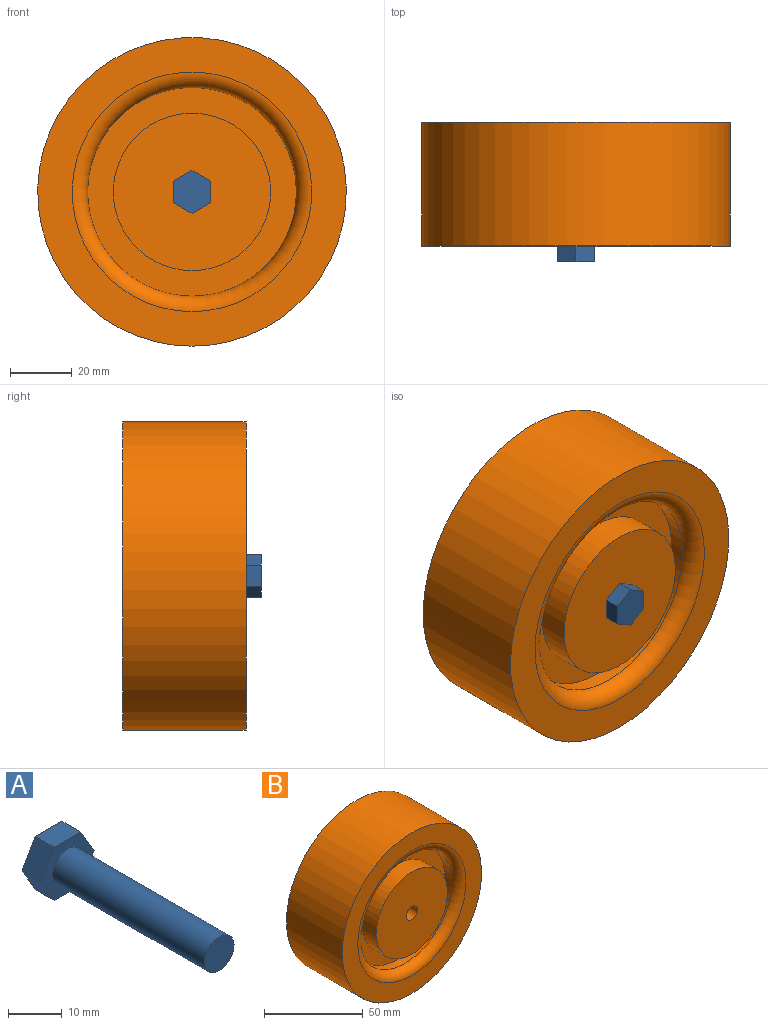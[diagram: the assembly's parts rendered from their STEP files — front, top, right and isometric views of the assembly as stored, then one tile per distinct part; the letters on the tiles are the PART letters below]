
ASSEMBLY  parts=2 mates=1
PART A: 10 faces, bbox 14x45x12.1 mm
  f0: plane 6.07x5mm, normal (-0.87,0,-0.5), area 35mm2, adj f1,f5,f6,f7
  f1: plane 7.01x5mm, normal (0,0,-1), area 35mm2, adj f0,f2,f6,f7
  f2: plane 6.07x5mm, normal (0.87,0,-0.5), area 35mm2, adj f1,f3,f6,f7
  f3: plane 6.07x5mm, normal (0.87,0,0.5), area 35mm2, adj f2,f4,f6,f7
  f4: plane 7.01x5mm, normal (0,0,1), area 35mm2, adj f3,f5,f6,f7
  f5: plane 6.07x5mm, normal (-0.87,0,0.5), area 35mm2, adj f0,f4,f6,f7
  f6: plane 14.01x12.13mm, normal (0,1,0), area 127.5mm2, adj f0,f1,f2,f3,f4,f5
  f7: plane 14.01x12.13mm, normal (0,-1,0), area 79.7mm2, adj f0,f1,f2,f3,f4,f5,f8
  f8: cylinder r=3.9mm len=40mm, axis (0,1,0), area 980.2mm2, adj f7,f9
  f9: plane 7.8x7.8mm, normal (0,-1,0), area 47.8mm2, adj f8
PART B: 9 faces, bbox 100x40x100 mm
  f0: cylinder r=50mm len=100mm, axis (0,1,0), area 12566.4mm2, adj f1,f2
  f1: plane 100x100mm, normal (0,-1,0), area 3124.1mm2, adj f0,f7
  f2: plane 100x100mm, normal (0,1,0), area 7803.7mm2, adj f0,f8
  f3: cylinder r=33.8mm len=67.6mm, axis (0,-1,0), area 1061.9mm2, adj f4,f7
  f4: plane 67.6x67.6mm, normal (0,-1,0), area 1546mm2, adj f3,f5
  f5: cylinder r=25.5mm len=51.01mm, axis (0,1,0), area 1602.5mm2, adj f4,f6
  f6: plane 51.01x51.01mm, normal (0,-1,0), area 1993.2mm2, adj f5,f8
  f7: torus R=38.8mm, axis (0,-1,0), area 1757.7mm2, adj f1,f3
  f8: cylinder r=4mm len=40mm, axis (0,-1,0), area 1005.3mm2, adj f2,f6
PLACE A rot(axis=(0.71,0,0.71),180deg) t=(-15.88,-11.31,-11.09)mm
PLACE B rot(axis=(0,-1,0),0deg) t=(-15.88,28.69,-11.09)mm fixed
MATE slider A.f8 <-> B.f5  axis (0,1,0) through (-15.88,28.69,-11.09)mm
